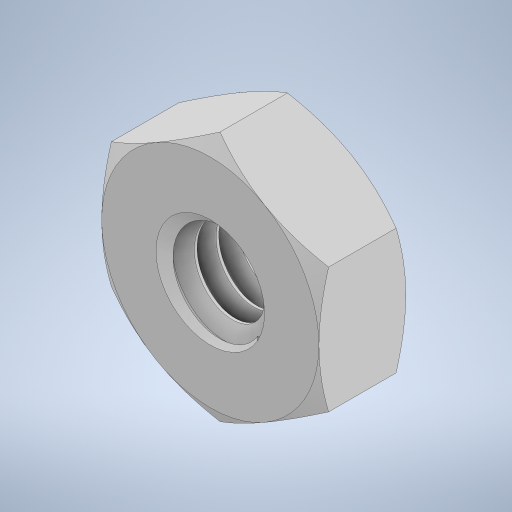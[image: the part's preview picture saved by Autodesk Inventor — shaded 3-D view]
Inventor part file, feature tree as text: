
AUTODESK INVENTOR PART (.ipt)
format: ipt  version: 2024 (Build 280153000, 153)  size: 396,288 bytes
history: native  units: mm
features: other x1, mirror x1
ambient origin geometry x8: Origin, YZ Plane, XZ Plane, XY Plane, X Axis, Y Axis, Z Axis, Center Point
bodies: Body1 (feature_tree)
feature tree (2):
  other  "Těleso1"
  mirror  "Mirror2"
